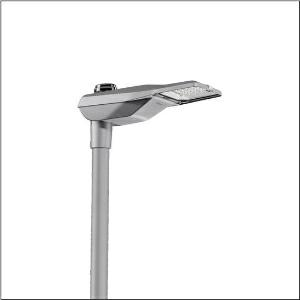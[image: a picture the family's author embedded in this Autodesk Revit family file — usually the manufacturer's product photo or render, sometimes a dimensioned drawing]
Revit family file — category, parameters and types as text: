
# Revit family: streetlight_sl_21_micro___st0_8a_5xe5c47n08cb_5e3b
name_source: partatom
category: Lighting Fixtures
units: mm (PartAtom-declared; Revit-internal decimal feet)

## family parameters
Cut with Voids When Loaded = No
Host = Face
Light Source = No
Part Type = Normal
Room Calculation Point = No
Round Connector Dimension = Use Diameter
Shared = No

## types (1)
- --- (1 x LED, 2380 lm, 15.8 W, 4000K)
    Apparent Load = 16 VA
    CIE Flux Codes = 38 75 97 100 100
    Color Rendering = 70
    Color Temperature = 4000K
    Default Elevation = 1800 mm
    Description = Streetlight SL 21 micro, mast luminaire, primary light control with lens, of PMMA, primary optical cover: cover, of toughened safety glass, transparent, light distribution: ST0.8a, light emission: direct distribution, primary light characteristic: asymmetric, installation type: post-top, LED, 3G 1.5mm², High Power LED, rated luminous flux: 2.380lm, luminous efficacy: 151lm/W, light colour: 740, colour temperature: 4000K, control gear: NEMA (7pin), control: overheat protection, pre-setting: linear dimming characteristic, constant luminous flux control, time-dependent luminous flux control, flexible luminous flux parameterisation, mains connection: 230..240V, AC, 50/60Hz, connection cable pre-assembled, cable length: 6,5m, wiring characteristics: H07RN-F, start of lifetime: 16W, end of service life: 16W, reduction: 8W, luminaire housing, of diecast aluminium (EN AC-44300), powder-coated, Siteco® metallic grey (DB 702S), corrosivity category C5 mid according to DIN EN ISO 12944, multi-level sealing system, sealing non-destructively replaceable, inclination adjustable: 0°, 5°, 10°, 15°, length: 528mm, width: 235mm, height: 110mm, spigot size: 76/60mm (post-top), mounting height: 4..8m, protection rating (complete): IP66, insulation class (complete): insulation class I (protective earthing), certification: CE, ENEC, ENEC+, VDE, impact resistance: IK09, permissible operating ambient temperature for outdoor applications: -40..+50°C, standard-compliant lighting for roads and squares, packaging unit: 1 piece

Light Distribution: ST0.8a
    Height = 110 mm
    Lamp = 1 x LED
    Lamp Light Flux = 2380 lm
    Lamp Power = 15.8 W
    Lamp count = 1
    Length = 528 mm
    Luminous efficacy = 151 lm/W
    Manufacturer = Siteco
    ModVariant = No
    Model = 5XE5C47N08CB
    Number of Poles = 1
    OnlyDefault = Yes
    Power Factor = 1
    Product Name = Streetlight SL 21 micro | ST0.8a
    Product group = mast luminaire | pylon top
    ProductGroupID = 6100
    Protection Class = Protection class I
    Protection Degree = IP 66
    RLX_Detail_Level = 1
    RLX_Emergency_Light_Flux = 0 lm
    RLX_Emergency_Type = 0
    RLX_Emergency_Type_DB = No
    RlxData = <blob elided: 98349 chars, md5=b4f42944>
    Socket = socket
    Standby Power = 0 W
    System Light Flux = 2380 lm
    System Power = 16 W
    Type Comments = factory setting: luminous flux: 100 % | dim-lin: 254 | 300 mA
    Type Image = l_1294375.jpg
    URL = http://relux.com
    VarID = @adj_129648
    Voltage = 0 V
    Weight = 0.00 kg
    Width = 235 mm

## geometry (parser evidence)
native form markers: Blend x4, Sweep x10
no freeform markers — native parametric forms only
